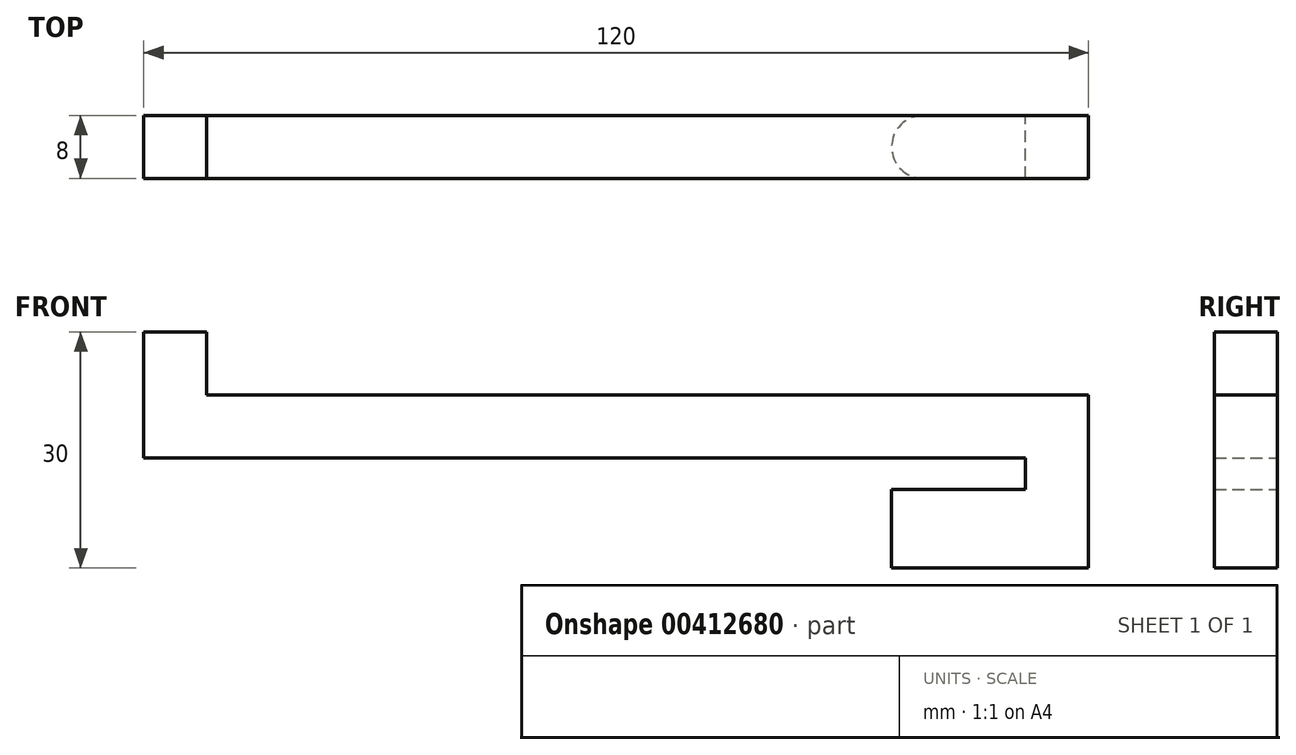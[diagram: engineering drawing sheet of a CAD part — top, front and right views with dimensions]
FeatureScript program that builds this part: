
annotation { "Feature Type Name" : "Feature", "Feature Type Description" : "" }
export const myFeature = defineFeature(function(context is Context, id is Id, definition is map)
    precondition{}
    {
        {
            var Q0;
            Q0=qCreatedBy(makeId("Right.planeOp"),FACE);
            var sketch = newSketch(context, id + "F0", { "sketchPlane" : qUnion([Q0])});
            skLineSegment(sketch, "E0.bottom", {"start": v(4, 4) * mm, "end": v(-4, 4) * mm});
            skLineSegment(sketch, "E0.top", {"start": v(4, -4) * mm, "end": v(-4, -4) * mm});
            skLineSegment(sketch, "E0.left", {"start": v(4, 4) * mm, "end": v(4, -4) * mm});
            skLineSegment(sketch, "E0.right", {"start": v(-4, 4) * mm, "end": v(-4, -4) * mm});
            skPoint(sketch, "E0.middle", {"position": v(0, 0) * mm});
            skSolve(sketch);
        }
        {
            var Q0;
            Q0 = qSketchRegion(id + "F0", true);
            extrude(context, id + "F1", {"entities" : qUnion([Q0]), "depth" : 120 * mm, "offsetDistance" : 25 * mm});
        }
        {
            var Q0;
            Q0=makeQuery(id+"F1.opExtrude","SWEPT_FACE",FACE,{"disambiguationData":[OSD([sQuery(id+"F0.wireOp",EDGE,"E0.bottom")])]});
            var sketch = newSketch(context, id + "F2", { "sketchPlane" : qUnion([Q0])});
            skLineSegment(sketch, "E1.bottom", {"start": v(0, -4) * mm, "end": v(8, -4) * mm});
            skLineSegment(sketch, "E1.top", {"start": v(0, 4) * mm, "end": v(8, 4) * mm});
            skLineSegment(sketch, "E1.left", {"start": v(0, -4) * mm, "end": v(0, 4) * mm});
            skLineSegment(sketch, "E1.right", {"start": v(8, -4) * mm, "end": v(8, 4) * mm});
            skSolve(sketch);
        }
        {
            var Q0;
            Q0=makeQuery(id+"F2.imprint","IMPRINT",FACE,{"disambiguationData":[TD([[makeQuery(id+"F2.imprint","IMPRINT",EDGE,{"derivedFrom":sQuery(id+"F2.wireOp",EDGE,"E1.bottom")}),-1.0]])]});
            extrude(context, id + "F3", {"entities" : qUnion([Q0]), "operationType" : NewBodyOperationType.ADD, "depth" : 8 * mm, "offsetDistance" : 25 * mm});
        }
        {
            var Q0;
            Q0=makeQuery(id+"F1.opExtrude","SWEPT_FACE",FACE,{"disambiguationData":[OSD([sQuery(id+"F0.wireOp",EDGE,"E0.top")])]});
            var sketch = newSketch(context, id + "F4", { "sketchPlane" : qUnion([Q0])});
            skLineSegment(sketch, "E2.bottom", {"start": v(120, 4) * mm, "end": v(112, 4) * mm});
            skLineSegment(sketch, "E2.top", {"start": v(120, -4) * mm, "end": v(112, -4) * mm});
            skLineSegment(sketch, "E2.left", {"start": v(120, 4) * mm, "end": v(120, -4) * mm});
            skLineSegment(sketch, "E2.right", {"start": v(112, 4) * mm, "end": v(112, -4) * mm});
            skSolve(sketch);
        }
        {
            var Q0;
            Q0=makeQuery(id+"F4.imprint","IMPRINT",FACE,{"disambiguationData":[TD([[makeQuery(id+"F4.imprint","IMPRINT",EDGE,{"derivedFrom":sQuery(id+"F4.wireOp",EDGE,"E2.bottom")}),1.0]])]});
            extrude(context, id + "F5", {"entities" : qUnion([Q0]), "operationType" : NewBodyOperationType.ADD, "depth" : 4 * mm, "offsetDistance" : 25 * mm});
        }
        {
            var Q0;
            Q0=makeQuery(id+"F5.opExtrude","CAP_FACE",FACE,{"disambiguationData":[OSD([sQuery(id+"F4.wireOp",EDGE,"E2.bottom"),sQuery(id+"F4.wireOp",EDGE,"E2.top"),sQuery(id+"F4.wireOp",EDGE,"E2.left"),sQuery(id+"F4.wireOp",EDGE,"E2.right")])],"isStart":false});
            var sketch = newSketch(context, id + "F6", { "sketchPlane" : qUnion([Q0])});
            skLineSegment(sketch, "E3.bottom", {"start": v(120, 4) * mm, "end": v(95, 4) * mm});
            skLineSegment(sketch, "E3.top", {"start": v(120, -4) * mm, "end": v(95, -4) * mm});
            skLineSegment(sketch, "E3.left", {"start": v(120, 4) * mm, "end": v(120, -4) * mm});
            skLineSegment(sketch, "E3.right", {"start": v(95, 4) * mm, "end": v(95, -4) * mm});
            skSolve(sketch);
        }
        {
            var Q0;
            {var subQ2=sQuery(id+"F6.wireOp",EDGE,"E3.right");Q0=makeQuery(id+"F6.imprint","IMPRINT",FACE,{"disambiguationData":[TD([[makeQuery(id+"F6.imprint","IMPRINT",EDGE,{"derivedFrom":subQ2}),1.0]])]});}
            var Q1;
            {var subQ0=sQuery(id+"F6.wireOp",EDGE,"E3.left");Q1=makeQuery(id+"F6.imprint","IMPRINT",FACE,{"disambiguationData":[TD([[makeQuery(id+"F6.imprint","IMPRINT",EDGE,{"derivedFrom":subQ0}),1.0]])]});}
            extrude(context, id + "F7", {"entities" : qUnion([Q0, Q1]), "operationType" : NewBodyOperationType.ADD, "depth" : 10 * mm, "offsetDistance" : 25 * mm});
        }
        {
            var Q0;
            Q0=makeQuery(id+"F7.opExtrude","SWEPT_EDGE",EDGE,{"disambiguationData":[OSD([sQuery(id+"F6.wireOp",EDGE,"E3.bottom"),sQuery(id+"F6.wireOp",EDGE,"E3.right")])]});
            var Q1;
            Q1=makeQuery(id+"F7.opExtrude","SWEPT_EDGE",EDGE,{"disambiguationData":[OSD([sQuery(id+"F6.wireOp",EDGE,"E3.top"),sQuery(id+"F6.wireOp",EDGE,"E3.right")])]});
            fillet(context, id + "F8", {"entities" : qUnion([Q0, Q1]), "radius" : 4 * mm, "tangentPropagation" : true, "allowEdgeOverflow" : false});
        }
    });
